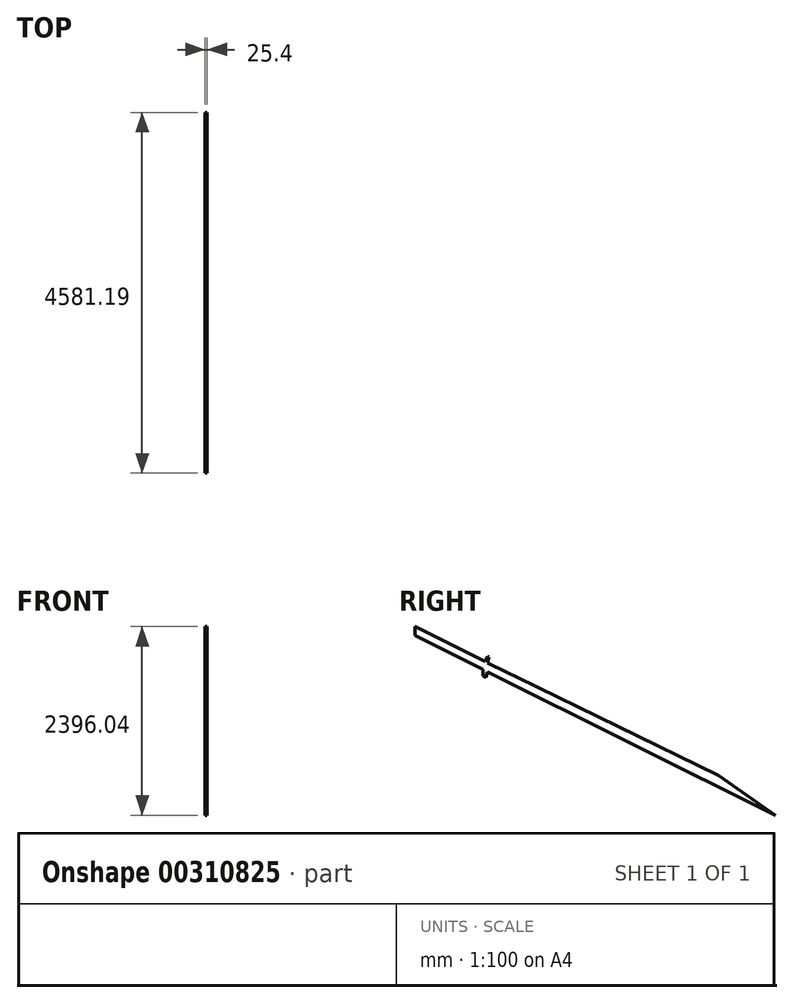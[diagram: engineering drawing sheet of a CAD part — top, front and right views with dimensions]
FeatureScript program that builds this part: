
annotation { "Feature Type Name" : "Feature", "Feature Type Description" : "" }
export const myFeature = defineFeature(function(context is Context, id is Id, definition is map)
    precondition{}
    {
        {
            var Q0;
            Q0=qCreatedBy(makeId("Right.planeOp"),FACE);
            var sketch = newSketch(context, id + "F0", { "sketchPlane" : qUnion([Q0])});
            skLineSegment(sketch, "E0", {"start": v(0, 0) * mm, "end": v(245.08, -122) * mm});
            skLineSegment(sketch, "E1", {"start": v(245.08, -122) * mm, "end": v(376.8, -187.71) * mm});
            skLineSegment(sketch, "E2", {"start": v(376.8, -187.71) * mm, "end": v(2934.51, -1431.59) * mm});
            skLineSegment(sketch, "E3", {"start": v(2934.51, -1431.59) * mm, "end": v(3657.25, -1936.1) * mm});
            skLineSegment(sketch, "E4", {"start": v(3657.25, -1936.1) * mm, "end": v(0, -115.5) * mm});
            skLineSegment(sketch, "E5", {"start": v(0, -115.5) * mm, "end": v(0, 0) * mm});
            skLineSegment(sketch, "E6", {"start": v(0, 0) * mm, "end": v(-923.94, 459.94) * mm});
            skLineSegment(sketch, "E7", {"start": v(-923.94, 459.94) * mm, "end": v(0, -115.5) * mm});
            skLineSegment(sketch, "E8", {"start": v(0, -115.5) * mm, "end": v(-923.94, 344.44) * mm});
            skLineSegment(sketch, "E9", {"start": v(-923.94, 344.44) * mm, "end": v(-923.94, 459.94) * mm});
            skLineSegment(sketch, "E10", {"start": v(0, 0) * mm, "end": v(17.6, 74.64) * mm});
            skLineSegment(sketch, "E11", {"start": v(17.6, 74.64) * mm, "end": v(0, 83.2) * mm});
            skLineSegment(sketch, "E12", {"start": v(0, 83.2) * mm, "end": v(-33.2, 16.52) * mm});
            skLineSegment(sketch, "E13", {"start": v(-33.2, 16.52) * mm, "end": v(-55.3, -87.97) * mm});
            skLineSegment(sketch, "E14", {"start": v(-55.3, -87.97) * mm, "end": v(-55.3, -170.54) * mm});
            skLineSegment(sketch, "E15", {"start": v(-55.3, -170.54) * mm, "end": v(-19.97, -187.71) * mm});
            skLineSegment(sketch, "E16", {"start": v(-19.97, -187.71) * mm, "end": v(0, -115.5) * mm});
            skSolve(sketch);
        }
        {
            var Q0;
            Q0 = qSketchRegion(id + "F0", true);
            extrude(context, id + "F1", {"entities" : qUnion([Q0]), "depth" : 25.4 * mm});
        }
    });
